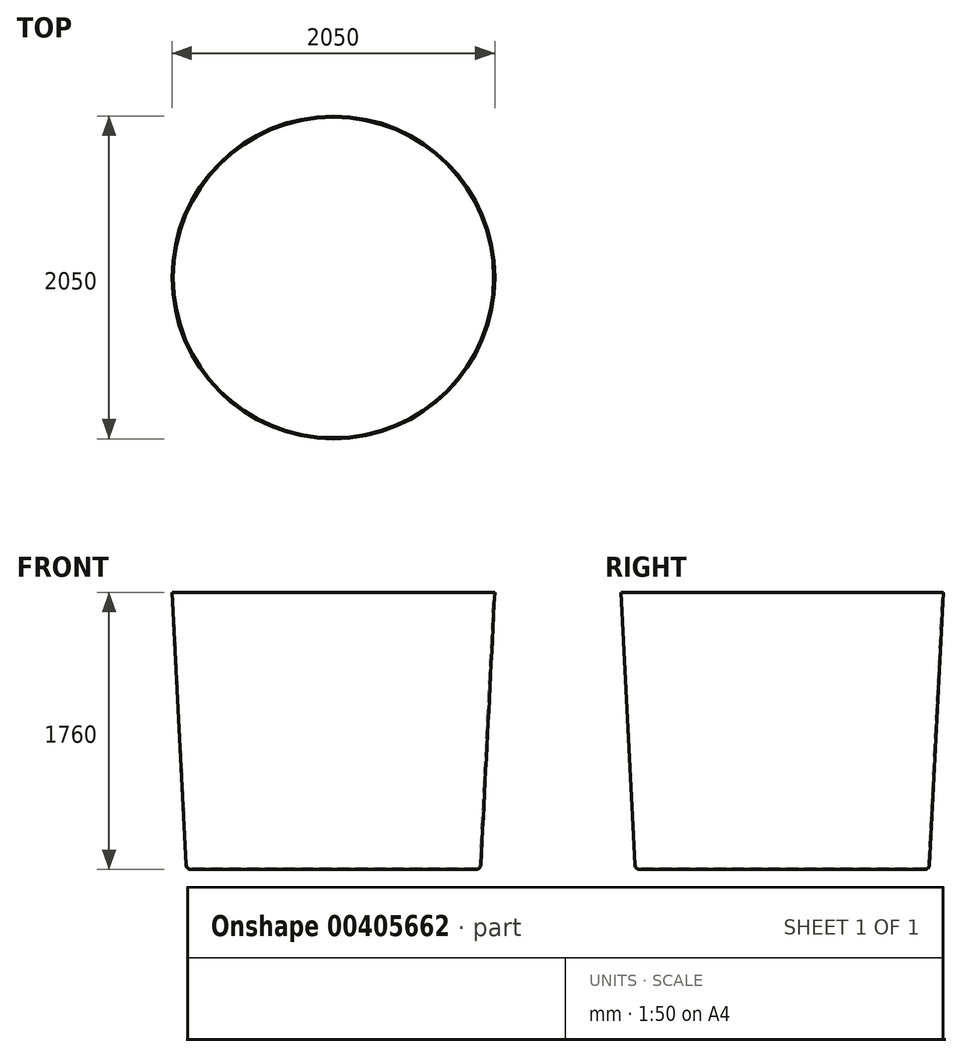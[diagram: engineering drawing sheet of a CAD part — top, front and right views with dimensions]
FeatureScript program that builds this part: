
annotation { "Feature Type Name" : "Feature", "Feature Type Description" : "" }
export const myFeature = defineFeature(function(context is Context, id is Id, definition is map)
    precondition{}
    {
        {
            var Q0;
            Q0=qCreatedBy(makeId("Top.planeOp"),FACE);
            var sketch = newSketch(context, id + "F0", { "sketchPlane" : qUnion([Q0])});
            skCircle(sketch, "E0", {"center": v(0, 0) * mm, "radius": 935 * mm});
            skSolve(sketch);
        }
        {
            var Q0;
            Q0=makeQuery(id+"F0.imprint","IMPRINT",FACE,{"disambiguationData":[TD([[makeQuery(id+"F0.imprint","IMPRINT",EDGE,{"derivedFrom":sQuery(id+"F0.wireOp",EDGE,"E0")}),1.0]])]});
            cPlane(context, id + "F1", {"entities" : qUnion([Q0]), "cplaneType" : CPlaneType.OFFSET, "offset" : 1760 * mm, "width" : 150 * mm, "height" : 150 * mm});
        }
        {
            var Q0;
            Q0=qCreatedBy(id+"F1.planeOp",FACE);
            var sketch = newSketch(context, id + "F2", { "sketchPlane" : qUnion([Q0])});
            skCircle(sketch, "E1", {"center": v(0, 0) * mm, "radius": 1025 * mm});
            skSolve(sketch);
        }
        {
            var Q0;
            Q0=makeQuery(id+"F2.imprint","IMPRINT",FACE,{"disambiguationData":[TD([[makeQuery(id+"F2.imprint","IMPRINT",EDGE,{"derivedFrom":sQuery(id+"F2.wireOp",EDGE,"E1")}),1.0]])]});
            var Q1;
            Q1=makeQuery(id+"F0.imprint","IMPRINT",FACE,{"disambiguationData":[TD([[makeQuery(id+"F0.imprint","IMPRINT",EDGE,{"derivedFrom":sQuery(id+"F0.wireOp",EDGE,"E0")}),1.0]])]});
            loft(context, id + "F3", {"sheetProfilesArray" : [{ "sheetProfileEntities" : qUnion([Q0]) }, { "sheetProfileEntities" : qUnion([Q1]) }]});
        }
        {
            var Q0;
            Q0=makeQuery(id+"F3.opLoft","MID_CAP_EDGE",EDGE,{"disambiguationData":[OSD([sQuery(id+"F0.wireOp",EDGE,"E0"),sQuery(id+"F2.wireOp",EDGE,"E1")])],"capPos":1.0});
            fillet(context, id + "F4", {"entities" : qUnion([Q0]), "radius" : 30 * mm, "tangentPropagation" : true, "allowEdgeOverflow" : false});
        }
        {
            var Q0;
            Q0=makeQuery(id+"F3.opLoft","CAP_FACE",FACE,{"disambiguationData":[OSD([makeQuery(id+"F2.imprint","IMPRINT",FACE,{"disambiguationData":[TD([[makeQuery(id+"F2.imprint","IMPRINT",EDGE,{"derivedFrom":sQuery(id+"F2.wireOp",EDGE,"E1")}),1.0]])]})])],"isStart":true});
            shell(context, id + "F5", {"entities" : qUnion([Q0]), "thickness" : 7 * mm});
        }
    });
